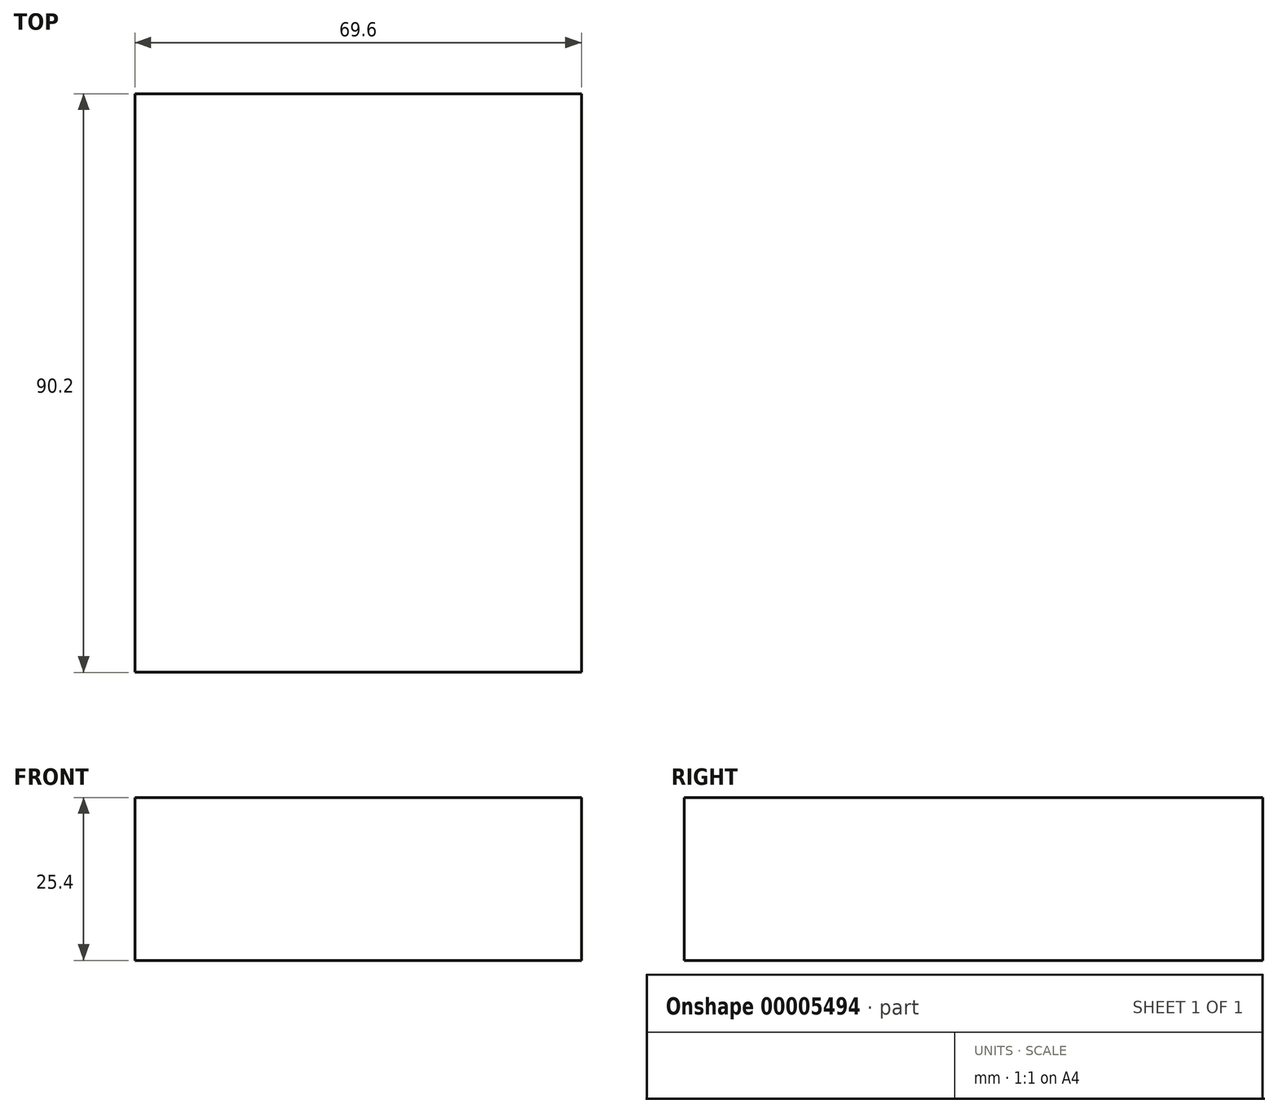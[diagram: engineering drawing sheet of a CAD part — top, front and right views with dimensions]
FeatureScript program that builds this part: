
annotation { "Feature Type Name" : "Feature", "Feature Type Description" : "" }
export const myFeature = defineFeature(function(context is Context, id is Id, definition is map)
    precondition{}
    {
        {
            var Q0;
            Q0=qCreatedBy(makeId("Top.planeOp"),FACE);
            var sketch = newSketch(context, id + "F0", { "sketchPlane" : qUnion([Q0])});
            skLineSegment(sketch, "E0.rect.bottom", {"start": v(34.8, 45.1) * mm, "end": v(-34.8, 45.1) * mm});
            skLineSegment(sketch, "E0.rect.top", {"start": v(34.8, -45.1) * mm, "end": v(-34.8, -45.1) * mm});
            skLineSegment(sketch, "E0.rect.left", {"start": v(34.8, 45.1) * mm, "end": v(34.8, -45.1) * mm});
            skLineSegment(sketch, "E0.rect.right", {"start": v(-34.8, 45.1) * mm, "end": v(-34.8, -45.1) * mm});
            skPoint(sketch, "E0.rect.middle", {"position": v(0, 0) * mm});
            skSolve(sketch);
        }
        {
            var Q0;
            Q0=makeQuery(id+"F0.imprint","IMPRINT",FACE,{"disambiguationData":[TD([[makeQuery(id+"F0.imprint","IMPRINT",EDGE,{"derivedFrom":sQuery(id+"F0.wireOp",EDGE,"E0.rect.bottom")}),1.0]])]});
            extrude(context, id + "F1", {"entities" : qUnion([Q0]), "depth" : 25.4 * mm});
        }
    });
